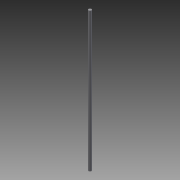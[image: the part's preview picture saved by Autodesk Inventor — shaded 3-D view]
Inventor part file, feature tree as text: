
AUTODESK INVENTOR PART (.ipt)
format: ipt  version: 2013 SP2 (Build 170200200, 200)  size: 59,904 bytes
history: native  units: mm
features: extrude x1, sketch x1
ambient origin geometry x8: Origin, YZ Plane, XZ Plane, XY Plane, X Axis, Y Axis, Z Axis, Center Point
bodies: Solid1 (feature_tree)
feature tree (2):
  extrude  "Extrusion1"  Depth=150.0mm TaperAngle=0.0deg
  sketch  "Sketch1"  dims[d0=3.0mm d1=150.0mm d2=0.0mm]
